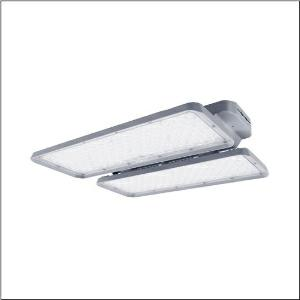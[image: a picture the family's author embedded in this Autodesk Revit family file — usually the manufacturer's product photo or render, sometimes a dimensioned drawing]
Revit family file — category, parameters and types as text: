
# Revit family: highbay_21-l_51hk41db4qca
name_source: partatom
category: Lighting Fixtures
units: mm (PartAtom-declared; Revit-internal decimal feet)

## family parameters
Cut with Voids When Loaded = No
Host = Face
Light Source = No
Part Type = Normal
Room Calculation Point = No
Round Connector Dimension = Use Diameter
Shared = No

## types (1)
- Highbay 21-L (1 x LED, 35600 lm, 200 W, 4000K)
    Apparent Load = 200 VA
    CIE Flux Codes = 87 97 99 100 100
    Color Rendering = 80
    Color Temperature = 4000K
    Default Elevation = 1800 mm
    Description = Highbay 21-L, LED high bay luminaire, primary light control with lens, of PC, light emission: direct distribution, primary light characteristic: symmetric, installation type: suspended mounting, surface-mounted, LED, rated luminous flux: 35.600lm, luminous efficacy: 178lm/W, light colour: 840, colour temperature: 4000K, with terminal, 5-pole, max. 2.5mm², mains connection: 220..240V, AC, 50Hz, rated input power: 200W, housing, of diecast aluminium, coated, grey, length: 471mm, width: 390mm, height: 87mm, protection rating (complete): IP66, insulation class (complete): insulation class I (protective earthing), certification: CE, ENEC, UKCA, protection symbol: D, impact resistance: IK08, permissible operating ambient temperature: -30..+60°C, corresponds to IFS (International Featured Standards) requirements for safety and quality in the food industry, LABS conformity tested according to VDMA 24364:2018-05, packaging unit: 1 piece
    Height = 89 mm
    Lamp = 1 x LED
    Lamp Light Flux = 35600 lm
    Lamp Power = 200 W
    Lamp count = 1
    Length = 471 mm
    Luminous efficacy = 178 lm/W
    Manufacturer = Siteco
    ModVariant = No
    Model = 51HK41DB4QCA
    Mounting Place = Ceiling
    Mounting Type = Pendant
    Number of Poles = 1
    OnlyDefault = Yes
    Power Factor = 1
    Product Name = Highbay 21-L
    Product group = LED high bay luminaire
    ProductGroupID = 903
    Protection Class = Protection class I
    Protection Degree = IP 66
    RLX_Detail_Level = 1
    RLX_Emergency_Light_Flux = 0 lm
    RLX_Emergency_Type = 0
    RLX_Emergency_Type_DB = No
    RlxData = <blob elided: 25429 chars, md5=192708ad>
    Socket = socket
    Standby Power = 0 W
    System Light Flux = 35600 lm
    System Power = 200 W
    Type Comments = Product without accessories
    Type Image = l_1276530.jpg
    URL = http://relux.com
    VarID = ---
    Voltage = 0 V
    Weight = 0.00 kg
    Width = 390 mm

## geometry (parser evidence)
native form markers: Blend x4, Sweep x10
no freeform markers — native parametric forms only
